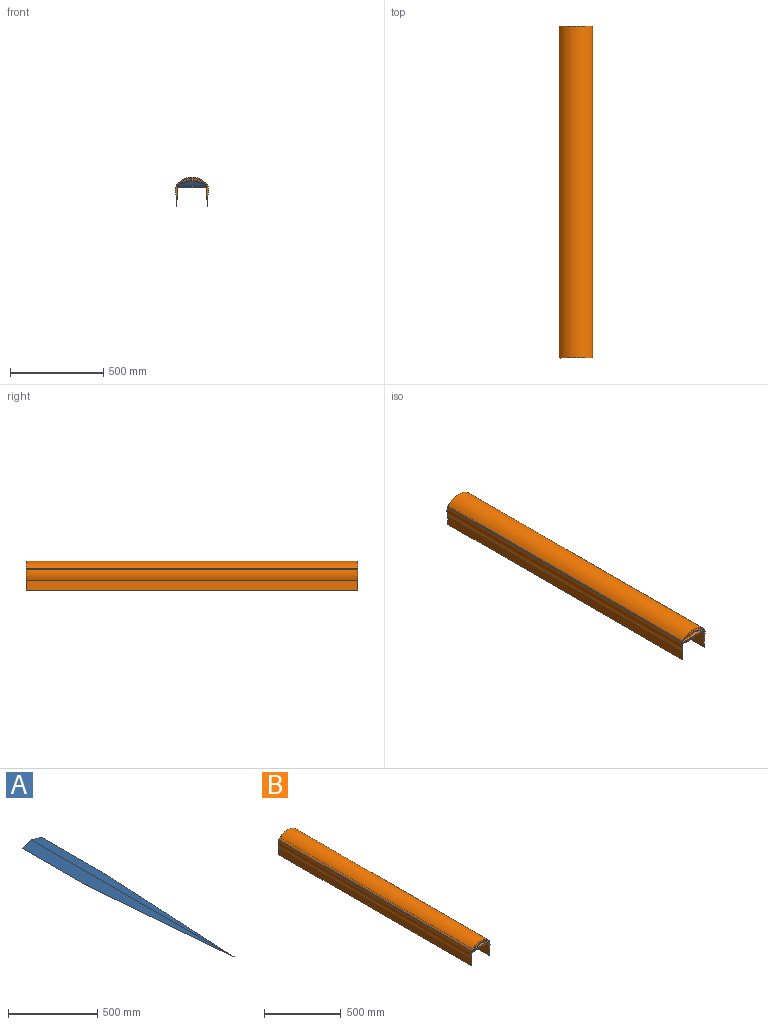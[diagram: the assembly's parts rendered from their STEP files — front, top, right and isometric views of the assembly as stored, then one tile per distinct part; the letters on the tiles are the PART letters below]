
ASSEMBLY  parts=2 mates=1
PART A: 5 faces, bbox 152.4x1599.4x19.1 mm
  f0: plane 508x152.4mm, normal (0,0,-1), area 77419.2mm2, adj f1,f2,f3,f4
  f1: plane 1599.37x76.2mm, normal (0.24,0,0.97), area 82762mm2, adj f0,f2,f3,f4
  f2: plane 1599.37x76.2mm, normal (-0.24,0,0.97), area 82762mm2, adj f0,f1,f3,f4
  f3: plane 1091.37x152.4mm, normal (0,-0.02,-1), area 83175.3mm2, adj f0,f1,f2
  f4: plane 152.4x19.05mm, normal (0,1,0), area 1451.6mm2, adj f0,f1,f2
PART B: 27 faces, bbox 177.8x1778x157.7 mm
  f0: plane 177.8x157.72mm, normal (0,-1,0), area 4417.7mm2, adj f1,f2,f3,f4,f5,f6,f7,f8
  f1: plane 1778x81.2mm, normal (-0.26,0,-0.97), area 149540.5mm2, adj f0,f2,f16,f17
  f2: plane 1778x2.62mm, normal (0,0,1), area 4657.2mm2, adj f0,f1,f3,f17
  f3: plane 1778x3.48mm, normal (-1,0,0), area 6195.7mm2, adj f0,f2,f4,f17
  f4: plane 1778x157.16mm, normal (0,0,1), area 279434.9mm2, adj f0,f3,f5,f17
  f5: plane 1778x3.48mm, normal (1,0,0), area 6195.7mm2, adj f0,f4,f6,f17
  f6: plane 1778x2.62mm, normal (0,0,1), area 4657.2mm2, adj f0,f5,f16,f17
  f7: cylinder r=88.9mm len=1778mm, axis (0,-1,0), area 111218.8mm2, adj f0,f8,f15,f17
  f8: cylinder r=109.22mm len=1778mm, axis (0,-1,0), area 339776.4mm2, adj f0,f7,f9,f17
  f9: plane 1778x3.48mm, normal (-0.95,0,0.31), area 6525mm2, adj f0,f8,f10,f17
  f10: cylinder r=88.9mm len=1778mm, axis (0,-1,0), area 104693.4mm2, adj f0,f9,f11,f17
  f11: plane 1778x57.26mm, normal (-1,0,-0.03), area 101854.8mm2, adj f0,f10,f12,f17
  f12: plane 1778x102.44mm, normal (1,0,-0.02), area 182182.4mm2, adj f0,f11,f13,f17
  f13: plane 1778x157.69mm, normal (0,0,-1), area 280366.9mm2, adj f0,f12,f14,f17
  f14: plane 1778x102.44mm, normal (-1,0,-0.02), area 182180.4mm2, adj f0,f13,f15,f17
  f15: plane 1778x57.26mm, normal (1,0,-0.03), area 101854.8mm2, adj f0,f7,f14,f17
  f16: plane 1778x81.2mm, normal (0.26,0,-0.97), area 149540.5mm2, adj f0,f1,f6,f17
  f17: plane 177.8x157.72mm, normal (0,1,0), area 5923.5mm2, adj f1,f2,f3,f4,f5,f6,f7,f8
  f18: plane 1772.92x163.45mm, normal (0,0,1), area 289788.5mm2, adj f0,f19,f20,f22
  f19: cylinder r=83.82mm len=1772.92mm, axis (0,-1,0), area 4451.6mm2, adj f0,f18,f21,f22
  f20: cylinder r=83.82mm len=1772.92mm, axis (0,-1,0), area 4451.6mm2, adj f0,f18,f21,f22
  f21: plane 1772.92x162.26mm, normal (0,0,-1), area 287681.3mm2, adj f0,f19,f20,f22
  f22: plane 163.45x2.44mm, normal (0,-1,0), area 397.3mm2, adj f18,f19,f20,f21
  f23: plane 1772.92x68.05mm, normal (0.26,0,0.97), area 124955mm2, adj f0,f24,f25,f26
  f24: cylinder r=104.14mm len=1772.92mm, axis (0,-1,0), area 262940.7mm2, adj f0,f23,f25,f26
  f25: plane 1772.92x68.05mm, normal (-0.26,0,0.97), area 124955mm2, adj f0,f23,f24,f26
  f26: plane 136.09x25.3mm, normal (0,-1,0), area 1108.5mm2, adj f23,f24,f25
PLACE A rot(axis=(-0.75,-0.66,0),0deg) t=(-14.39,1618.54,-7.15)mm
PLACE B rot(axis=(-0.75,-0.66,0),0deg) t=(-14.39,-15.18,-6.15)mm fixed
MATE slider A.f4 <-> B.f0  axis (0,1,0) through (-14.39,1618.54,11.9)mm
